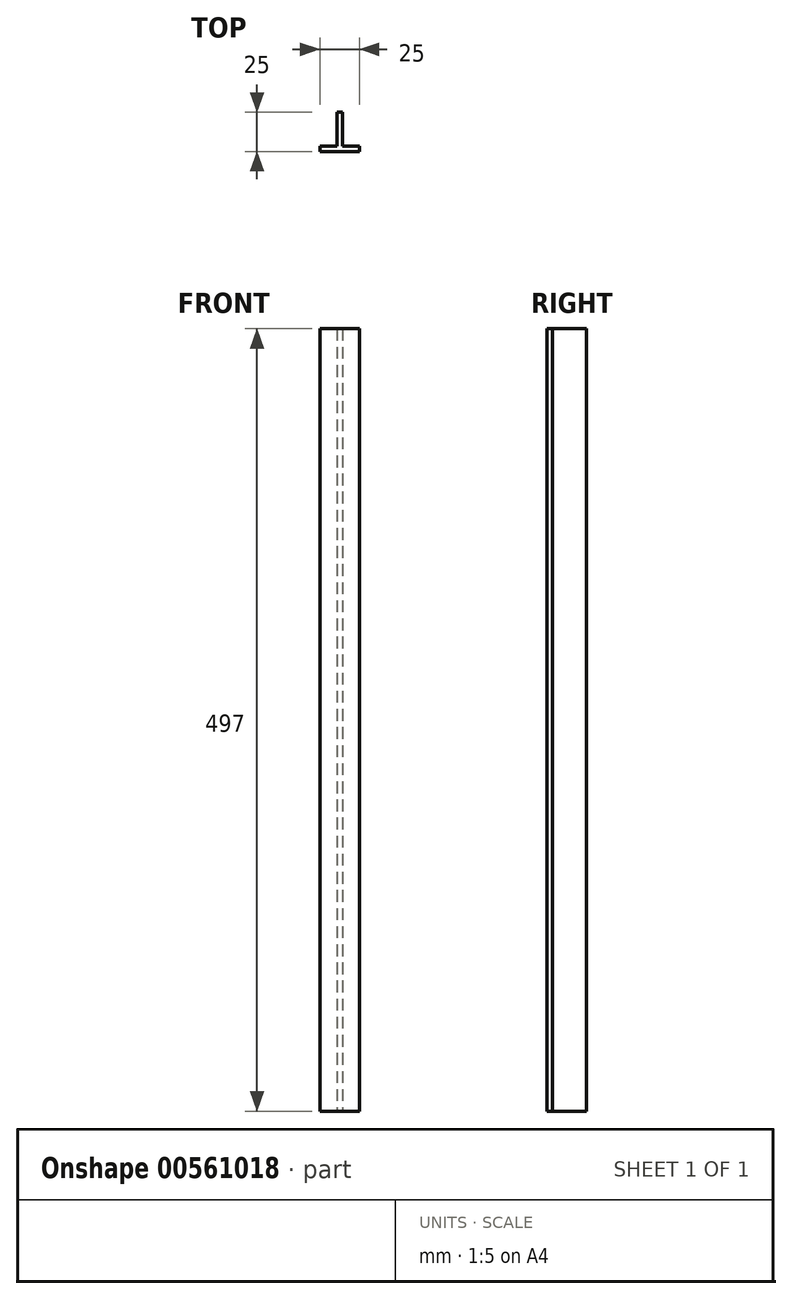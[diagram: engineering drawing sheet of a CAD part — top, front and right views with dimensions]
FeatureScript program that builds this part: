
annotation { "Feature Type Name" : "Feature", "Feature Type Description" : "" }
export const myFeature = defineFeature(function(context is Context, id is Id, definition is map)
    precondition{}
    {
        {
            var Q0;
            Q0=qCreatedBy(makeId("Top.planeOp"),FACE);
            var sketch = newSketch(context, id + "F0", { "sketchPlane" : qUnion([Q0])});
            skLineSegment(sketch, "E0", {"start": v(-14.25, -3.5) * mm, "end": v(10.75, -3.5) * mm});
            skLineSegment(sketch, "E1", {"start": v(10.75, -3.5) * mm, "end": v(10.75, 0) * mm});
            skLineSegment(sketch, "E2", {"start": v(10.75, 0) * mm, "end": v(0, 0) * mm});
            skLineSegment(sketch, "E3", {"start": v(0, 0) * mm, "end": v(0, 21.5) * mm});
            skLineSegment(sketch, "E4", {"start": v(0, 21.5) * mm, "end": v(-3.5, 21.5) * mm});
            skLineSegment(sketch, "E5", {"start": v(-3.5, 21.5) * mm, "end": v(-3.5, 0) * mm});
            skLineSegment(sketch, "E6", {"start": v(-14.25, 0) * mm, "end": v(-14.25, -3.5) * mm});
            skLineSegment(sketch, "E7", {"start": v(-3.5, 0) * mm, "end": v(-14.25, 0) * mm});
            skSolve(sketch);
        }
        {
            var Q0;
            Q0 = qSketchRegion(id + "F0", true);
            extrude(context, id + "F1", {"entities" : qUnion([Q0]), "depth" : 497 * mm, "offsetDistance" : 25 * mm});
        }
    });
